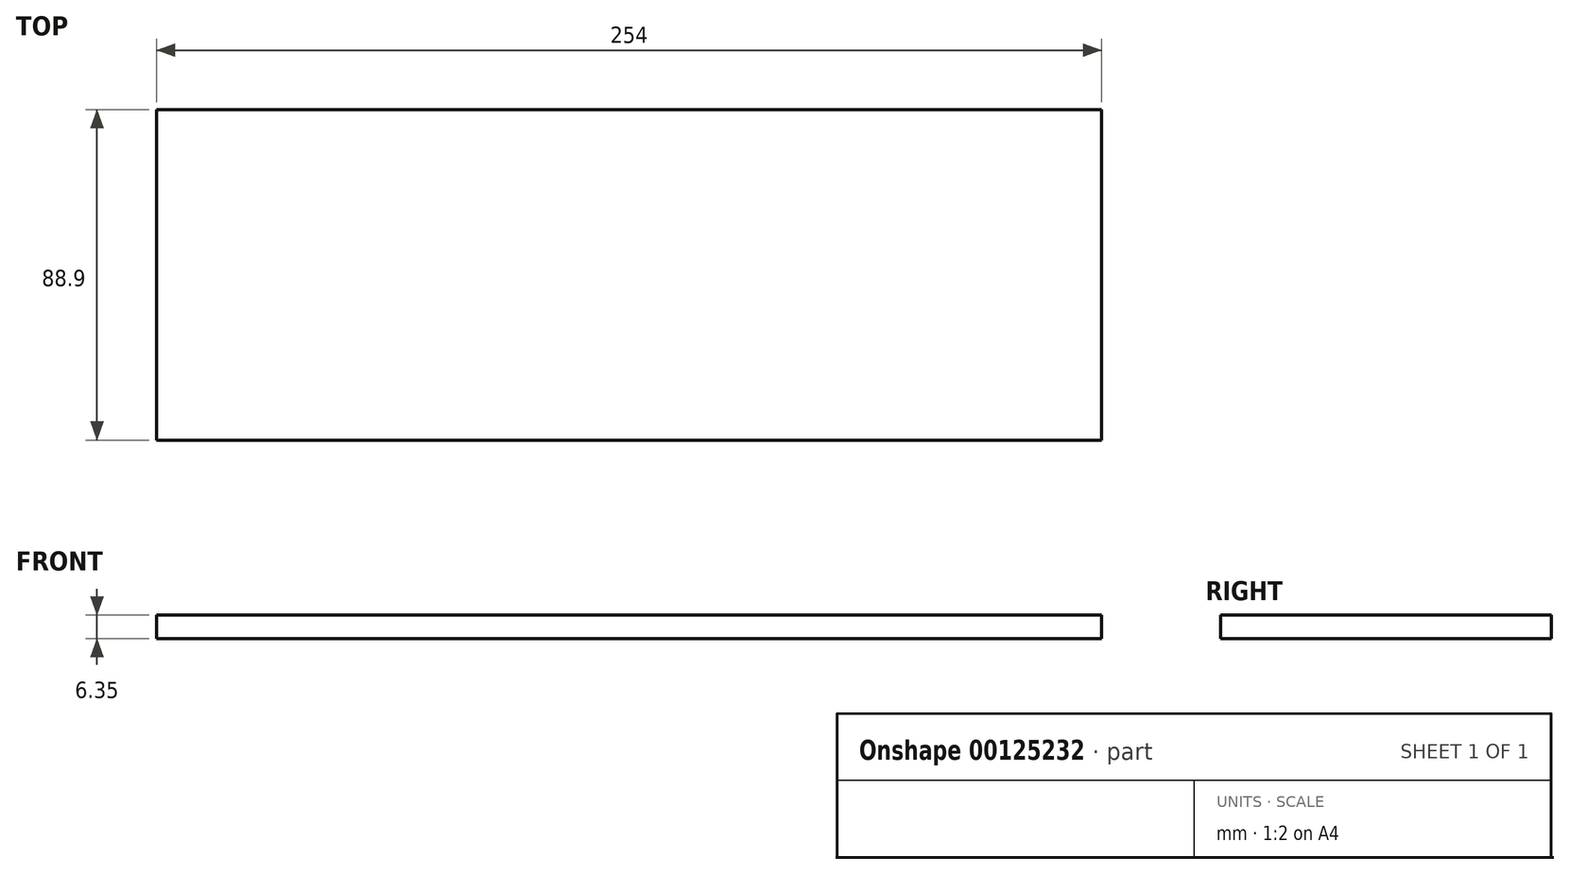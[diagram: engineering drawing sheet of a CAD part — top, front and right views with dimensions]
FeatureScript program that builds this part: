
annotation { "Feature Type Name" : "Feature", "Feature Type Description" : "" }
export const myFeature = defineFeature(function(context is Context, id is Id, definition is map)
    precondition{}
    {
        {
            var Q0;
            Q0=qCreatedBy(makeId("Top.planeOp"),FACE);
            var sketch = newSketch(context, id + "F0", { "sketchPlane" : qUnion([Q0])});
            skLineSegment(sketch, "E0.bottom", {"start": v(-127.77, -31.06) * mm, "end": v(126.23, -31.06) * mm});
            skLineSegment(sketch, "E0.top", {"start": v(-127.77, -119.96) * mm, "end": v(126.23, -119.96) * mm});
            skLineSegment(sketch, "E0.left", {"start": v(-127.77, -31.06) * mm, "end": v(-127.77, -119.96) * mm});
            skLineSegment(sketch, "E0.right", {"start": v(126.23, -31.06) * mm, "end": v(126.23, -119.96) * mm});
            skSolve(sketch);
        }
        {
            var Q0;
            Q0=makeQuery(id+"F0.imprint","IMPRINT",FACE,{"disambiguationData":[TD([[makeQuery(id+"F0.imprint","IMPRINT",EDGE,{"derivedFrom":sQuery(id+"F0.wireOp",EDGE,"E0.bottom")}),-1.0]])]});
            extrude(context, id + "F1", {"entities" : qUnion([Q0]), "depth" : 6.35 * mm});
        }
    });
